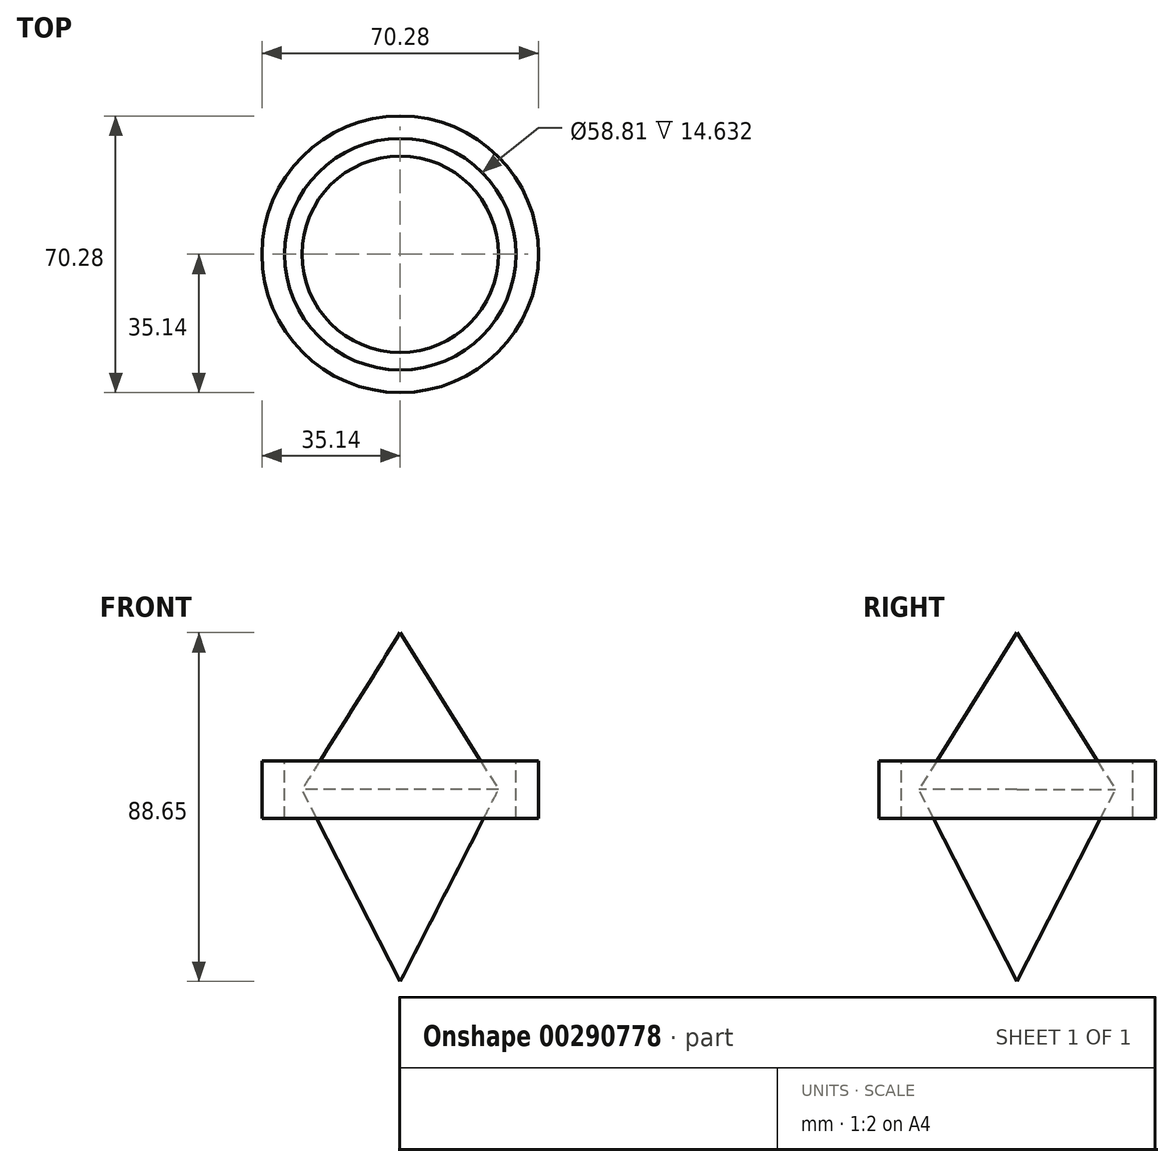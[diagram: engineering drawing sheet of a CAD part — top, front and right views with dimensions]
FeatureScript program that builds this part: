
annotation { "Feature Type Name" : "Feature", "Feature Type Description" : "" }
export const myFeature = defineFeature(function(context is Context, id is Id, definition is map)
    precondition{}
    {
        {
            var Q0;
            Q0=qCreatedBy(makeId("Front.planeOp"),FACE);
            var sketch = newSketch(context, id + "F0", { "sketchPlane" : qUnion([Q0])});
            skLineSegment(sketch, "E0", {"start": v(0, 39.88) * mm, "end": v(-24.96, 0) * mm});
            skLineSegment(sketch, "E1", {"start": v(-24.96, 0) * mm, "end": v(0, -48.77) * mm});
            skLineSegment(sketch, "E2", {"start": v(0, 39.88) * mm, "end": v(0, -48.77) * mm});
            skLineSegment(sketch, "E3.bottom", {"start": v(-35.14, 7.32) * mm, "end": v(-29.4, 7.32) * mm});
            skLineSegment(sketch, "E3.top", {"start": v(-35.14, -7.32) * mm, "end": v(-29.4, -7.32) * mm});
            skLineSegment(sketch, "E3.left", {"start": v(-35.14, 7.32) * mm, "end": v(-35.14, -7.32) * mm});
            skLineSegment(sketch, "E3.right", {"start": v(-29.4, 7.32) * mm, "end": v(-29.4, -7.32) * mm});
            skPoint(sketch, "E3.middle", {"position": v(-32.28, 0) * mm});
            skSolve(sketch);
        }
        {
            var Q0;
            Q0=makeQuery(id+"F0.imprint","IMPRINT",FACE,{"disambiguationData":[TD([[makeQuery(id+"F0.imprint","IMPRINT",EDGE,{"derivedFrom":sQuery(id+"F0.wireOp",EDGE,"E0")}),1.0]])]});
            var Q1;
            Q1=sQuery(id+"F0.wireOp",EDGE,"E2");
            revolve(context, id + "F1", {"entities" : qUnion([Q0]), "axis" : qUnion([Q1]), "revolveType" : RevolveType.FULL});
        }
        {
            var Q0;
            Q0=makeQuery(id+"F0.imprint","IMPRINT",FACE,{"disambiguationData":[TD([[makeQuery(id+"F0.imprint","IMPRINT",EDGE,{"derivedFrom":sQuery(id+"F0.wireOp",EDGE,"E3.bottom")}),-1.0]])]});
            var Q1;
            Q1=sQuery(id+"F0.wireOp",EDGE,"E2");
            revolve(context, id + "F2", {"entities" : qUnion([Q0]), "axis" : qUnion([Q1]), "revolveType" : RevolveType.FULL});
        }
    });
